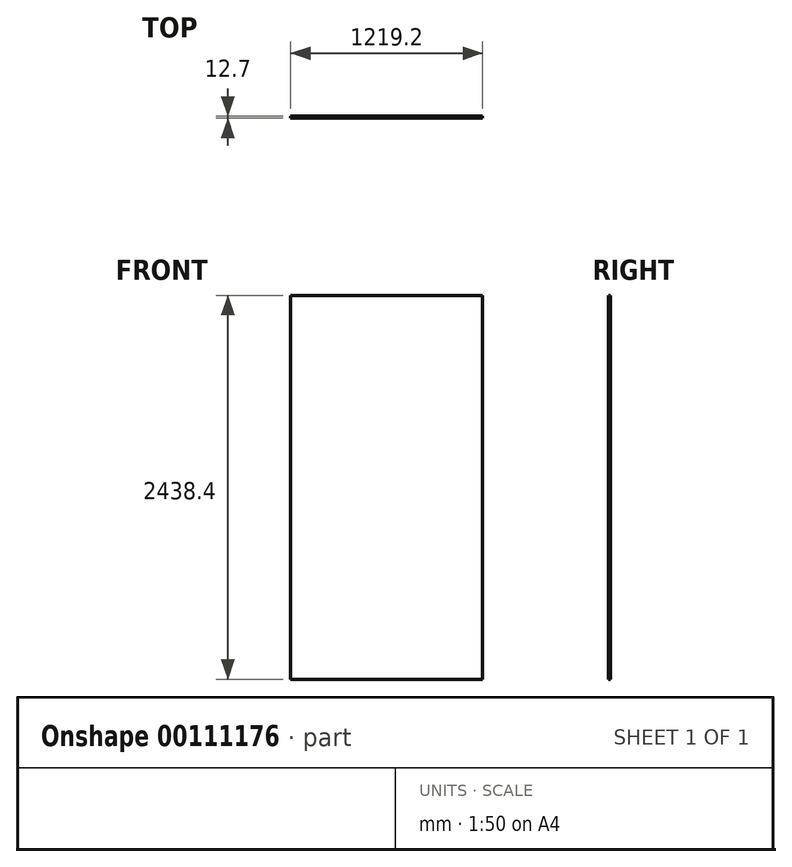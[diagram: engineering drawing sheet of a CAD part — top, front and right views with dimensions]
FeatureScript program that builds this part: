
annotation { "Feature Type Name" : "Feature", "Feature Type Description" : "" }
export const myFeature = defineFeature(function(context is Context, id is Id, definition is map)
    precondition{}
    {
        {
            var Q0;
            Q0=qCreatedBy(makeId("Front.planeOp"),FACE);
            var sketch = newSketch(context, id + "F0", { "sketchPlane" : qUnion([Q0])});
            skPoint(sketch, "E0.middle", {"position": v(0, 0) * mm});
            skLineSegment(sketch, "E1", {"start": v(-50.8, -101.6) * mm, "end": v(-50.8, 101.6) * mm});
            skLineSegment(sketch, "E2", {"start": v(-50.8, 101.6) * mm, "end": v(50.8, 101.6) * mm});
            skLineSegment(sketch, "E3", {"start": v(50.8, 101.6) * mm, "end": v(50.8, -101.6) * mm});
            skLineSegment(sketch, "E4", {"start": v(50.8, -101.6) * mm, "end": v(-50.8, -101.6) * mm});
            skSolve(sketch);
        }
        {
            var Q0;
            Q0=makeQuery(id+"F0.imprint","IMPRINT",FACE,{"disambiguationData":[TD([[makeQuery(id+"F0.imprint","IMPRINT",EDGE,{"derivedFrom":sQuery(id+"F0.wireOp",EDGE,"E1")}),-1.0]])]});
            extrude(context, id + "F1", {"entities" : qUnion([Q0]), "endBound" : BoundingType.SYMMETRIC, "depth" : 12.7 * mm});
        }
        {
            var Q0;
            Q0=makeQuery(id+"F1.opExtrude","SWEPT_FACE",FACE,{"disambiguationData":[OSD([sQuery(id+"F0.wireOp",EDGE,"E3")])]});
            extrude(context, id + "F2", {"entities" : qUnion([Q0]), "operationType" : NewBodyOperationType.ADD, "depth" : 1117.6 * mm});
        }
        {
            var Q0;
            {var subQ0=sQuery(id+"F0.wireOp",EDGE,"E2");Q0=makeQuery(id+"F2.boolean.opBoolean","MERGE",FACE,{"derivedFrom":[makeQuery(id+"F1.opExtrude","SWEPT_FACE",FACE,{"disambiguationData":[OSD([subQ0])]}),makeQuery(id+"F2.opExtrude","SWEPT_FACE",FACE,{"disambiguationData":[OSD([subQ0,sQuery(id+"F0.wireOp",EDGE,"E3")])]})]});}
            extrude(context, id + "F3", {"entities" : qUnion([Q0]), "operationType" : NewBodyOperationType.ADD, "depth" : 2235.2 * mm});
        }
    });
